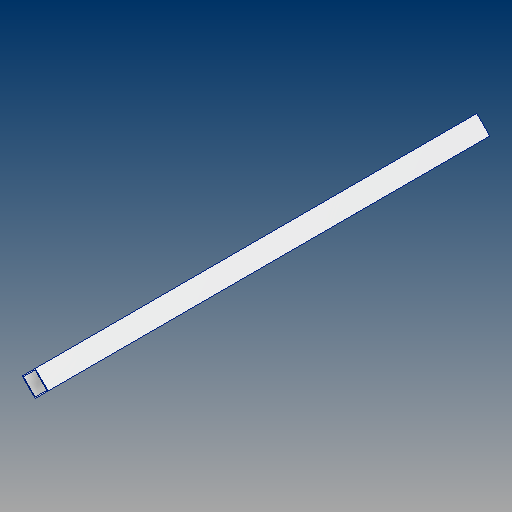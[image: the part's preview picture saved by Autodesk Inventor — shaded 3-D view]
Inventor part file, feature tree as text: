
AUTODESK INVENTOR PART (.ipt)
format: ipt  version: 2020 (Build 240168000, 168)  size: 89,088 bytes
history: native  units: in
note: dims shown in document units (in); Inventor stores cm internally (conversion verified against a paired STEP export)
features: extrude x1, shell x1, sketch x1
ambient origin geometry x8: Origin, YZ Plane, XZ Plane, XY Plane, X Axis, Y Axis, Z Axis, Center Point
bodies: Solid1 (feature_tree)
feature tree (3):
  extrude  "Extrusion1"  Depth=1.0in
  shell  "Shell1"  Thickness=24.0in
  sketch  "Sketch1"  dims[d2=1.0in d3=1.0in d4=24.0in d5=0.0in d6=0.05in]
